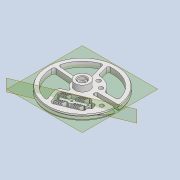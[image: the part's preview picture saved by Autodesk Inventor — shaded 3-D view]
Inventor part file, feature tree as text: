
AUTODESK INVENTOR PART (.ipt)
format: ipt  version: 2020 (Build 240168000, 168)  size: 1,905,152 bytes
history: native  units: mm
features: sketch x21, extrude x20, projected_geometry x18, fillet x14, thicken_offset x9, chamfer x6, other x3, pattern_linear x2, plane x2, revolve x1, mirror x1, reference x1
ambient origin geometry x8: Origin, YZ Plane, XZ Plane, XY Plane, X Axis, Y Axis, Z Axis, Center Point
bodies: Solid1 (feature_tree)
feature tree (98):
  extrude  "Extrusion1"  Depth=3.0mm TaperAngle=0.0deg
  revolve  "Revolution1"  [1 undecoded]
  extrude  "Extrusion2"  Depth=6.0mm
  extrude  "Extrusion3"  Depth=11.0mm
  extrude  "Extrusion4"  Depth=34.0mm
  extrude  "Extrusion5"  Depth=14.0mm
  chamfer  "Chamfer1"  Distance=5.0mm
  fillet  "Fillet1"  Radius=2.5mm
  fillet  "Fillet2"  Radius=15.0mm
  extrude  "Extrusion6"  Depth=0.5mm
  extrude  "Extrusion7"  TaperAngle=45.0deg  [1 undecoded]
  extrude  "Extrusion8"  Depth=12.0mm
  pattern_linear  "Rectangular Pattern1"  Count1=2  [1 undecoded]
  pattern_linear  "Rectangular Pattern2"  Spacing1=3.5mm  [1 undecoded]
  thicken_offset  "Thicken1"
  chamfer  "Chamfer2"  Distance=0.4mm
  plane  "Work Plane1"
  mirror  "Mirror1"
  extrude  "Extrusion9"  Depth=0.5mm TaperAngle=0.0deg
  fillet  "Fillet3"  Radius=40.0mm
  fillet  "Fillet4"  Radius=10.0mm
  fillet  "Fillet5"  Radius=1.0mm
  fillet  "Fillet6"  Radius=1.0mm
  extrude  "Extrusion10"  Depth=1.0mm TaperAngle=45.0deg
  fillet  "Fillet7"  Radius=5.0mm
  chamfer  "Chamfer3"  Distance=4.0mm
  extrude  "Extrusion11"  Depth=0.5mm TaperAngle=0.0deg
  fillet  "Fillet8"  Radius=2.0mm
  thicken_offset  "Thicken2"
  fillet  "Fillet9"  Radius=2.0mm
  extrude  "Extrusion12"  Depth=1.0mm
  thicken_offset  "Thicken3"
  thicken_offset  "Thicken4"
  chamfer  "Chamfer4"  Distance=0.5mm
  plane  "Work Plane2"
  extrude  "Extrusion13"  Depth=1.5mm
  chamfer  "Chamfer5"  Distance=3.0mm
  extrude  "Extrusion14"  Depth=0.5mm
  extrude  "Extrusion15"  Depth=0.5mm TaperAngle=0.0deg
  fillet  "Fillet10"  Radius=0.2mm
  fillet  "Fillet11"  Radius=0.5mm
  fillet  "Fillet12"  Radius=1.5mm
  thicken_offset  "Thicken5"
  thicken_offset  "Thicken6"
  thicken_offset  "Thicken7"
  extrude  "Extrusion16"  Depth=0.5mm
  extrude  "Extrusion17"  Depth=0.5mm
  extrude  "Extrusion18"  Depth=0.5mm TaperAngle=0.0deg
  extrude  "Extrusion19"  Depth=1.0mm
  thicken_offset  "Thicken8"
  thicken_offset  "Thicken9"
  extrude  "Extrusion20"  Depth=0.5mm
  fillet  "Fillet13"  Radius=5.0mm
  fillet  "Fillet14"  Radius=0.5mm
  chamfer  "Chamfer6"  Distance=7.3mm
  sketch  "Sketch1"  dims[d0=50.0mm d1=3.0mm d2=0.0mm]
  sketch  "Sketch2"  dims[d3=1.5mm d4=1.5mm]
  projected_geometry  "Projected Loop1"
  sketch  "Sketch3"  dims[d5=90.0deg d6=6.0mm]
  sketch  "Sketch4"  dims[d7=3.0mm d8=0.0mm d9=11.0mm]
  projected_geometry  "Projected Loop2"
  sketch  "Sketch5"  dims[d10=5.0mm d11=0.0mm d12=34.0mm]
  projected_geometry  "Projected Loop3"
  sketch  "Sketch6"  dims[d13=3.0mm d14=14.0mm d15=5.0mm d16=0.0mm d17=2.5mm d18=15.0mm d19=0.0mm]
  projected_geometry  "Projected Loop4"
  sketch  "Sketch7"  dims[d20=0.5mm d21=2.0mm d22=45.0deg d23=0.5mm]
  projected_geometry  "Projected Loop5"
  sketch  "Sketch8"  dims[d24=1.0mm d25=45.0deg]
  projected_geometry  "Projected Loop6"
  sketch  "Sketch9"  dims[d26=3.0mm d27=12.0mm d28=20.0mm]
  projected_geometry  "Projected Loop7"
  projected_geometry  "Projected Loop8"
  sketch  "Sketch10"  dims[d29=15.0mm d30=0.0mm]
  projected_geometry  "Projected Loop9"
  sketch  "Sketch11"  dims[d31=4.0mm]
  projected_geometry  "Projected Loop10"
  sketch  "Sketch12"  dims[d32=4.0mm]
  projected_geometry  "Projected Loop11"
  sketch  "Sketch13"  dims[d33=2.0mm]
  projected_geometry  "Projected Loop12"
  sketch  "Sketch14"  dims[d34=14.0mm]
  reference  "Reference1"
  sketch  "Sketch15"  dims[d35=3.0mm d36=0.0mm]
  projected_geometry  "Projected Loop13"
  sketch  "Sketch16"  dims[d37=3.0mm]
  projected_geometry  "Projected Loop14"
  sketch  "Sketch17"  dims[d38=0.5mm]
  sketch  "Sketch18"  dims[d39=0.5mm]
  sketch  "Sketch19"  dims[d40=2.2mm]
  projected_geometry  "Projected Loop15"
  projected_geometry  "Projected Loop16"
  sketch  "Sketch20"  dims[d41=3.5mm]
  projected_geometry  "Projected Loop17"
  sketch  "Sketch21"  dims[d42=0.4mm d43=3.5mm d44=0.4mm d45=3.0mm d46=0.0mm d47=40.0mm d49=1.3mm d50=20.0mm d52=10.0mm d53=1.0mm d54=1.0mm d55=1.0mm d56=2.0mm d57=45.0deg d58=5.0mm d59=4.0mm d60=3.0mm d61=0.0mm d62=2.0mm d63=2.0mm d64=1.0mm d65=0.5mm d66=1.5mm d67=3.0mm d68=3.0mm d69=3.0mm d70=0.0mm d71=0.2mm d72=0.5mm d73=2.0mm d74=45.0deg d75=1.5mm d76=1.4mm d77=1.4mm d78=3.0mm d79=0.0mm d80=1.0mm d81=5.0mm d82=5.0mm d83=0.5mm d84=7.3mm d85=7.330383mm d86=3.0mm d87=3.0mm d88=0.0mm d89=0.5mm d90=0.5mm d91=0.5mm d92=0.5mm d93=0.5mm d94=2.0mm d95=45.0deg d96=-2.0mm d97=1.0mm d98=4.5mm d99=0.0mm d100=1.0mm d101=2.0mm d102=45.0deg d103=6.108652mm d104=6.981317mm d105=10.0mm d106=3.1mm d107=10.0mm d108=3.1mm d109=4.5mm d110=0.0mm d111=18.0mm d112=46.0mm d113=2.5mm d114=2.5mm d115=2.5mm d116=2.5mm d117=26.0mm d118=3.0mm d119=4.712389mm d120=12.217305mm d121=4.5mm d122=0.0mm d123=4.0mm d124=1.0mm d125=1.5mm d126=2.0mm d127=2.0mm d128=2.0mm d129=2.0mm d130=1.0mm d131=1.0mm d132=4.5mm d133=0.0mm d134=3.0mm d135=4.5mm d136=0.0mm d137=12.0mm d138=25.481807mm d139=4.0mm d140=4.5mm d141=0.0mm d142=4.5mm d143=0.0mm d144=1.0mm d145=1.0mm d146=1.0mm d147=1.0mm d148=3.3mm d149=1.4mm d150=6.0mm d151=0.0mm d152=1.0mm d153=1.0mm d154=0.5mm d155=2.0mm d156=45.0deg]
  projected_geometry  "Projected Loop18"
  parser-record x1  (decoder bookkeeping rows leaked as tree rows — omitted from the tree; the rows remain in map.json)
  other  "driver_ass_1.iam"
  other  "bearing_3_6_2:1"
note: 4 required parameter values undecoded (feature->parameter linkage not recoverable at this tier; creation-order binding heuristic only, values carry confidence <= 0.55)
note: 1 file-system path scrubbed to <path> (originals preserved in map.json)